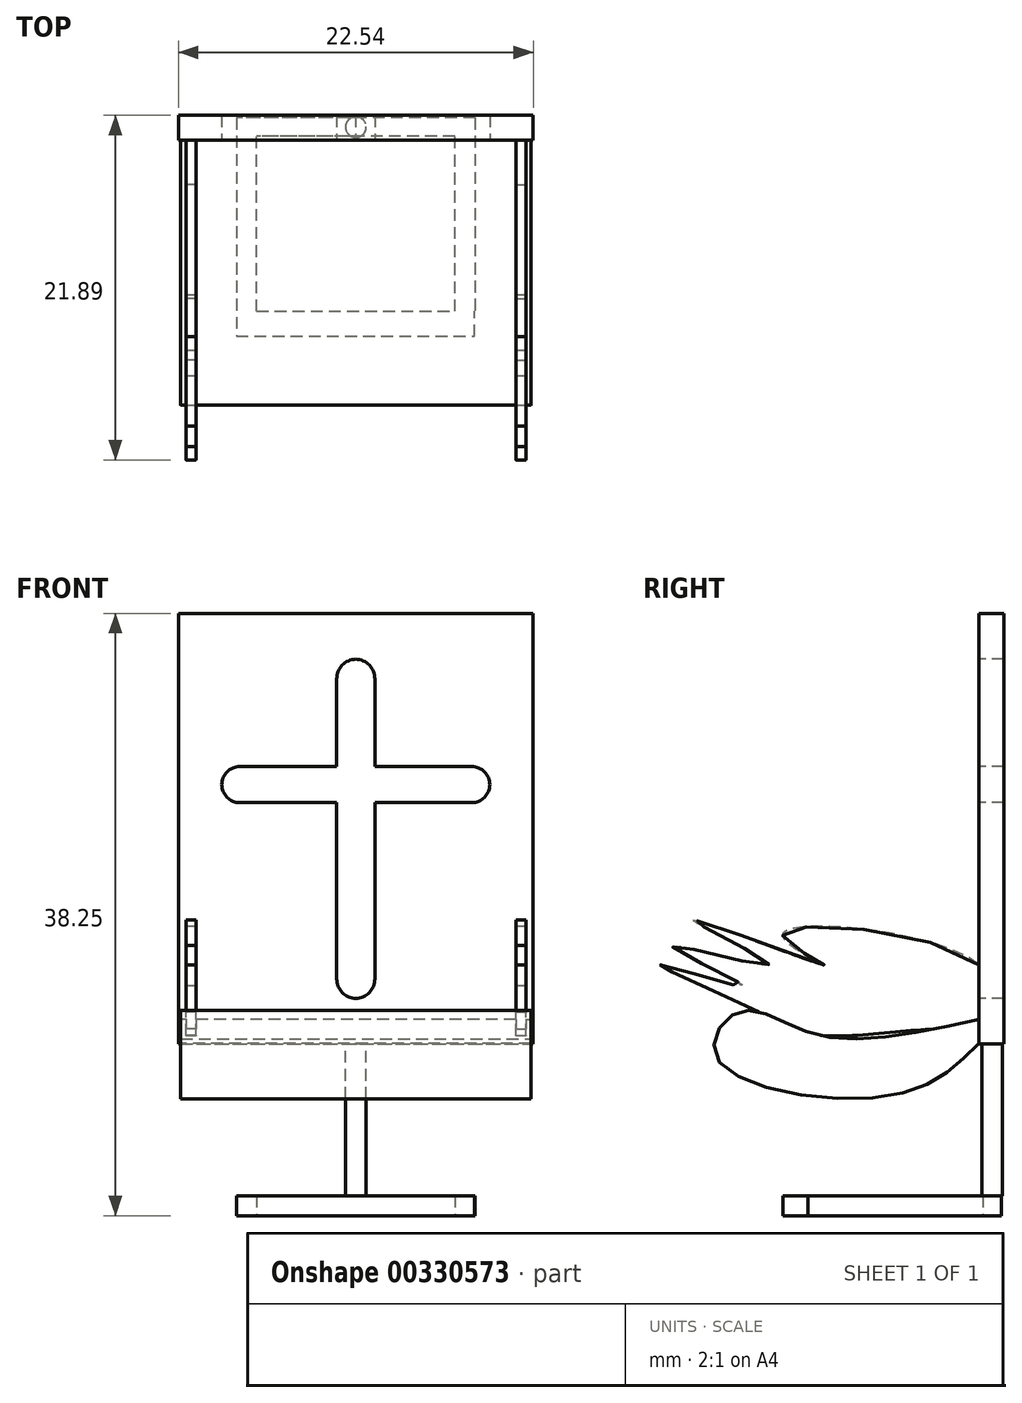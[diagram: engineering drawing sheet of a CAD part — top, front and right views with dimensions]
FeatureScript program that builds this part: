
annotation { "Feature Type Name" : "Feature", "Feature Type Description" : "" }
export const myFeature = defineFeature(function(context is Context, id is Id, definition is map)
    precondition{}
    {
        {
            var Q0;
            Q0=qCreatedBy(makeId("Front.planeOp"),FACE);
            var sketch = newSketch(context, id + "F0", { "sketchPlane" : qUnion([Q0])});
            skLineSegment(sketch, "E0.bottom", {"start": v(-45.08, -20.13) * mm, "end": v(43.82, -20.13) * mm});
            skLineSegment(sketch, "E0.left", {"start": v(-45.08, -20.13) * mm, "end": v(-45.08, 76.53) * mm});
            skLineSegment(sketch, "E0.right", {"start": v(43.82, -20.13) * mm, "end": v(43.82, 76.53) * mm});
            skLineSegment(sketch, "E1.top", {"start": v(43.82, 89.23) * mm, "end": v(-45.08, 89.23) * mm});
            skLineSegment(sketch, "E1.left", {"start": v(43.82, 76.53) * mm, "end": v(43.82, 89.23) * mm});
            skLineSegment(sketch, "E1.right", {"start": v(-45.08, 76.53) * mm, "end": v(-45.08, 89.23) * mm});
            skLineSegment(sketch, "E2.bottom", {"start": v(5.17, -3.58) * mm, "end": v(-4.84, -3.58) * mm});
            skLineSegment(sketch, "E2.left", {"start": v(5.17, -3.58) * mm, "end": v(5.17, 72.62) * mm});
            skLineSegment(sketch, "E2.right", {"start": v(-4.84, -3.58) * mm, "end": v(-4.84, 72.62) * mm});
            skLineSegment(sketch, "E3.bottom", {"start": v(29.78, 50.33) * mm, "end": v(-29.45, 50.33) * mm});
            skLineSegment(sketch, "E3.top", {"start": v(29.78, 41.17) * mm, "end": v(-29.45, 41.17) * mm});
            skLineSegment(sketch, "E3.left", {"start": v(29.78, 50.33) * mm, "end": v(29.78, 41.17) * mm});
            skLineSegment(sketch, "E3.right", {"start": v(-29.45, 50.33) * mm, "end": v(-29.45, 41.17) * mm});
            skPoint(sketch, "E3.middle", {"position": v(0.16, 45.75) * mm});
            skArc(sketch, "E4", {"start": v(-29.45, 50.33) * mm, "mid": v(-34.03, 45.75) * mm, "end": v(-29.45, 41.17) * mm});
            skArc(sketch, "E5", {"start": v(29.78, 41.17) * mm, "mid": v(34.36, 45.75) * mm, "end": v(29.78, 50.33) * mm});
            skArc(sketch, "E6", {"start": v(-4.84, -3.58) * mm, "mid": v(0.16, -8.58) * mm, "end": v(5.17, -3.58) * mm});
            skArc(sketch, "E7", {"start": v(5.17, 72.62) * mm, "mid": v(0.16, 77.63) * mm, "end": v(-4.84, 72.62) * mm});
            skSolve(sketch);
        }
        {
            var Q0;
            Q0=qCreatedBy(makeId("Right.planeOp"),FACE);
            var sketch = newSketch(context, id + "F1", { "sketchPlane" : qUnion([Q0])});
            skFitSpline(sketch, "E8", {"points": [v(0, -13.89) * mm, v(-41.84, -17.62) * mm, v(-60.64, -11.86) * mm, v(-66.74, -23.38) * mm, v(-22.87, -33.37) * mm, v(0, -19.99) * mm], "startDerivative": vector(-186.7, -41.76) * mm, "endDerivative": vector(87.3, 88.35) * mm});
            skLineSegment(sketch, "E9", {"start": v(0, -13.89) * mm, "end": v(0, -19.99) * mm});
            skSolve(sketch);
        }
        {
            var Q0;
            Q0=makeQuery(id+"F0.imprint","IMPRINT",FACE,{"disambiguationData":[TD([[makeQuery(id+"F0.imprint","IMPRINT",EDGE,{"derivedFrom":sQuery(id+"F0.wireOp",EDGE,"E0.bottom")}),1.0]])]});
            extrude(context, id + "F2", {"entities" : qUnion([Q0]), "oppositeDirection" : true, "depth" : 6.35 * mm});
        }
        {
            var Q0;
            Q0=makeQuery(id+"F1.imprint","IMPRINT",FACE,{"disambiguationData":[TD([[makeQuery(id+"F1.imprint","IMPRINT",EDGE,{"derivedFrom":sQuery(id+"F1.wireOp",EDGE,"E8")}),1.0]])]});
            extrude(context, id + "F3", {"entities" : qUnion([Q0]), "operationType" : NewBodyOperationType.ADD, "depth" : 43.18 * mm});
        }
        {
            var Q0;
            Q0=makeQuery(id+"F3.opExtrude","CAP_FACE",FACE,{"disambiguationData":[OSD([sQuery(id+"F1.wireOp",EDGE,"E8"),sQuery(id+"F1.wireOp",EDGE,"E9")])],"isStart":true});
            extrude(context, id + "F4", {"entities" : qUnion([Q0]), "operationType" : NewBodyOperationType.ADD, "depth" : 44.45 * mm});
        }
        {
            var Q0;
            Q0=makeQuery(id+"F2.opExtrude","SWEPT_FACE",FACE,{"disambiguationData":[OSD([sQuery(id+"F0.wireOp",EDGE,"E0.bottom")])]});
            var sketch = newSketch(context, id + "F5", { "sketchPlane" : qUnion([Q0])});
            skCircle(sketch, "E10", {"center": v(0, -3.38) * mm, "radius": 2.64 * mm});
            skSolve(sketch);
        }
        {
            var Q0;
            Q0 = qSketchRegion(id + "F5", true);
            extrude(context, id + "F6", {"entities" : qUnion([Q0]), "operationType" : NewBodyOperationType.ADD, "depth" : 38.55 * mm});
        }
        {
            var Q0;
            Q0=makeQuery(id+"F6.opExtrude","CAP_FACE",FACE,{"disambiguationData":[OSD([sQuery(id+"F5.wireOp",EDGE,"E10")])],"isStart":false});
            var sketch = newSketch(context, id + "F7", { "sketchPlane" : qUnion([Q0])});
            skLineSegment(sketch, "E11.bottom", {"start": v(30.33, -5.74) * mm, "end": v(-30.33, -5.74) * mm});
            skLineSegment(sketch, "E11.top", {"start": v(30.33, -1.02) * mm, "end": v(-30.33, -1.02) * mm});
            skLineSegment(sketch, "E11.left", {"start": v(30.33, -5.74) * mm, "end": v(30.33, -1.02) * mm});
            skLineSegment(sketch, "E11.right", {"start": v(-30.33, -5.74) * mm, "end": v(-30.33, -1.02) * mm});
            skPoint(sketch, "E11.middle", {"position": v(0, -3.38) * mm});
            skSolve(sketch);
        }
        {
            var Q0;
            {var subQ0=sQuery(id+"F7.wireOp",EDGE,"E11.right");Q0=makeQuery(id+"F7.imprint","IMPRINT",FACE,{"disambiguationData":[TD([[makeQuery(id+"F7.imprint","IMPRINT",EDGE,{"derivedFrom":subQ0}),-1.0]])]});}
            var Q1;
            {var subQ0=sQuery(id+"F7.wireOp",EDGE,"E11.left");Q1=makeQuery(id+"F7.imprint","IMPRINT",FACE,{"disambiguationData":[TD([[makeQuery(id+"F7.imprint","IMPRINT",EDGE,{"derivedFrom":subQ0}),1.0]])]});}
            var Q2;
            {var subQ0=sQuery(id+"F7.wireOp",EDGE,"E11.bottom");var subQ1=makeQuery(id+"F6.opExtrude","CAP_EDGE",EDGE,{"disambiguationData":[OSD([sQuery(id+"F5.wireOp",EDGE,"E10")])],"isStart":false});var subQ2=makeQuery(id+"F7.imprint","INTERSECT",VERTEX,{"disambiguationData":[OD(0.0)],"derivedFrom":[subQ1,subQ0]});Q2=makeQuery(id+"F7.imprint","IMPRINT",FACE,{"disambiguationData":[TD([[makeQuery(id+"F7.imprint","IMPRINT",EDGE,{"disambiguationData":[TD([[subQ2,-1.0]])],"derivedFrom":subQ0}),-1.0]])]});}
            extrude(context, id + "F8", {"entities" : qUnion([Q0, Q1, Q2]), "operationType" : NewBodyOperationType.ADD, "depth" : 5.08 * mm});
        }
        {
            var Q0;
            Q0=makeQuery(id+"F8.opExtrude","SWEPT_FACE",FACE,{"disambiguationData":[OSD([sQuery(id+"F7.wireOp",EDGE,"E11.top")])]});
            var sketch = newSketch(context, id + "F9", { "sketchPlane" : qUnion([Q0])});
            skLineSegment(sketch, "E12.bottom", {"start": v(-30.33, -58.68) * mm, "end": v(-25.22, -58.68) * mm});
            skLineSegment(sketch, "E12.top", {"start": v(-30.33, -63.76) * mm, "end": v(-25.22, -63.76) * mm});
            skLineSegment(sketch, "E12.left", {"start": v(-30.33, -58.68) * mm, "end": v(-30.33, -63.76) * mm});
            skLineSegment(sketch, "E12.right", {"start": v(-25.22, -58.68) * mm, "end": v(-25.22, -63.76) * mm});
            skLineSegment(sketch, "E13.bottom", {"start": v(30.33, -58.68) * mm, "end": v(25.3, -58.68) * mm});
            skLineSegment(sketch, "E13.top", {"start": v(30.33, -63.76) * mm, "end": v(25.3, -63.76) * mm});
            skLineSegment(sketch, "E13.left", {"start": v(30.33, -58.68) * mm, "end": v(30.33, -63.76) * mm});
            skLineSegment(sketch, "E13.right", {"start": v(25.3, -58.68) * mm, "end": v(25.3, -63.76) * mm});
            skSolve(sketch);
        }
        {
            var Q0;
            Q0=makeQuery(id+"F9.imprint","IMPRINT",FACE,{"disambiguationData":[TD([[makeQuery(id+"F9.imprint","IMPRINT",EDGE,{"derivedFrom":sQuery(id+"F9.wireOp",EDGE,"E12.bottom")}),1.0]])]});
            var Q1;
            Q1=makeQuery(id+"F9.imprint","IMPRINT",FACE,{"disambiguationData":[TD([[makeQuery(id+"F9.imprint","IMPRINT",EDGE,{"derivedFrom":sQuery(id+"F9.wireOp",EDGE,"E13.bottom")}),1.0]])]});
            extrude(context, id + "F10", {"entities" : qUnion([Q0, Q1]), "operationType" : NewBodyOperationType.ADD, "depth" : 44.45 * mm});
        }
        {
            var Q0;
            Q0=makeQuery(id+"F3.opExtrude","CAP_FACE",FACE,{"disambiguationData":[OSD([sQuery(id+"F1.wireOp",EDGE,"E8"),sQuery(id+"F1.wireOp",EDGE,"E9")])],"isStart":false});
            var sketch = newSketch(context, id + "F11", { "sketchPlane" : qUnion([Q0])});
            skFitSpline(sketch, "E14", {"points": [v(0, 0) * mm, v(-49.85, 7.37) * mm, v(-39.35, 0) * mm, v(-72.6, 11.3) * mm, v(-53.35, 0) * mm, v(-77.85, 4.74) * mm, v(-59.92, -5.32) * mm, v(-80.92, 0) * mm, v(-55.87, -11.97) * mm, v(-40.23, -18.01) * mm, v(-11.26, -16.32) * mm, v(0, -13.89) * mm, v(0, 0) * mm]});
            skSolve(sketch);
        }
        {
            var Q0;
            {var subQ0=sQuery(id+"F11.wireOp",EDGE,"E14");var subQ1=makeQuery(id+"F3.opExtrude","CAP_EDGE",EDGE,{"disambiguationData":[OSD([sQuery(id+"F1.wireOp",EDGE,"E8")])],"isStart":false});var subQ2=makeQuery(id+"F11.imprint","INTERSECT",VERTEX,{"disambiguationData":[OD(1.0)],"derivedFrom":[subQ1,subQ0]});Q0=makeQuery(id+"F11.imprint","IMPRINT",FACE,{"disambiguationData":[TD([[makeQuery(id+"F11.imprint","IMPRINT",EDGE,{"disambiguationData":[TD([[subQ2,-1.0]])],"derivedFrom":subQ0}),1.0]])]});}
            extrude(context, id + "F12", {"entities" : qUnion([Q0]), "operationType" : NewBodyOperationType.ADD, "oppositeDirection" : true, "depth" : 2.54 * mm});
        }
        {
            var Q0;
            Q0=makeQuery(id+"F2.opExtrude","SWEPT_BODY",BODY,{"disambiguationData":[OSD([sQuery(id+"F0.wireOp",EDGE,"E0.bottom"),sQuery(id+"F0.wireOp",EDGE,"E0.left"),sQuery(id+"F0.wireOp",EDGE,"E0.right"),sQuery(id+"F0.wireOp",EDGE,"E1.top"),sQuery(id+"F0.wireOp",EDGE,"E1.left"),sQuery(id+"F0.wireOp",EDGE,"E1.right"),sQuery(id+"F0.wireOp",EDGE,"d2293a8d-0336-4ec7-9d55-4d29c6c5a1e8.left"),sQuery(id+"F0.wireOp",EDGE,"d2293a8d-0336-4ec7-9d55-4d29c6c5a1e8.right"),sQuery(id+"F0.wireOp",EDGE,"3a96d54c-97b1-4134-b270-c8d69c560f2c.bottom"),sQuery(id+"F0.wireOp",EDGE,"3a96d54c-97b1-4134-b270-c8d69c560f2c.top"),sQuery(id+"F0.wireOp",EDGE,"50cf77b1-2162-471d-ace5-73bb84abd7fd"),sQuery(id+"F0.wireOp",EDGE,"1dc3a23f-0b35-4e5d-b878-b8cb4b9b89ba"),sQuery(id+"F0.wireOp",EDGE,"557aeda7-10cd-4d19-b53b-240f223889f2"),sQuery(id+"F0.wireOp",EDGE,"99ebc8af-5f9b-4179-b6f0-57f66800448b")])]});
            var Q1;
            Q1=qCreatedBy(makeId("Right.planeOp"),FACE);
            mirror(context, id + "F13", {"operationType" : NewBodyOperationType.ADD, "entities" : qUnion([Q0]), "mirrorPlane" : qUnion([Q1])});
        }
        {
            var Q0;
            Q0=makeQuery(id+"F10.opExtrude","CAP_FACE",FACE,{"disambiguationData":[OSD([sQuery(id+"F9.wireOp",EDGE,"E12.bottom"),sQuery(id+"F9.wireOp",EDGE,"E12.top"),sQuery(id+"F9.wireOp",EDGE,"E12.left"),sQuery(id+"F9.wireOp",EDGE,"E12.right")])],"isStart":false});
            var sketch = newSketch(context, id + "F14", { "sketchPlane" : qUnion([Q0])});
            skLineSegment(sketch, "E15.bottom", {"start": v(-30.33, -58.68) * mm, "end": v(30.21, -58.68) * mm});
            skLineSegment(sketch, "E15.top", {"start": v(-30.33, -63.76) * mm, "end": v(30.21, -63.76) * mm});
            skLineSegment(sketch, "E15.left", {"start": v(-30.33, -58.68) * mm, "end": v(-30.33, -63.76) * mm});
            skLineSegment(sketch, "E15.right", {"start": v(30.21, -58.68) * mm, "end": v(30.21, -63.76) * mm});
            skSolve(sketch);
        }
        {
            var Q0;
            Q0 = qSketchRegion(id + "F14", true);
            extrude(context, id + "F15", {"entities" : qUnion([Q0]), "operationType" : NewBodyOperationType.ADD, "depth" : 6.35 * mm});
        }
        {
            var Q0;
            Q0=makeQuery(id+"F2.opExtrude","SWEPT_BODY",BODY,{"disambiguationData":[OSD([sQuery(id+"F0.wireOp",EDGE,"E0.bottom"),sQuery(id+"F0.wireOp",EDGE,"E0.left"),sQuery(id+"F0.wireOp",EDGE,"E0.right"),sQuery(id+"F0.wireOp",EDGE,"E1.top"),sQuery(id+"F0.wireOp",EDGE,"E1.left"),sQuery(id+"F0.wireOp",EDGE,"E1.right"),sQuery(id+"F0.wireOp",EDGE,"E2.left"),sQuery(id+"F0.wireOp",EDGE,"E2.right"),sQuery(id+"F0.wireOp",EDGE,"E3.bottom"),sQuery(id+"F0.wireOp",EDGE,"E3.top"),sQuery(id+"F0.wireOp",EDGE,"E4"),sQuery(id+"F0.wireOp",EDGE,"E5"),sQuery(id+"F0.wireOp",EDGE,"E6"),sQuery(id+"F0.wireOp",EDGE,"E7")])]});
            var Q1;
            Q1=qCreatedBy(makeId("Origin.pointOp"),VERTEX);
            transform(context, id + "F16", {"entities" : qUnion([Q0]), "transformType" : TransformType.SCALE_UNIFORMLY, "scale" : .25, "scalePoint" : qUnion([Q1]), "makeCopy" : false});
        }
    });
